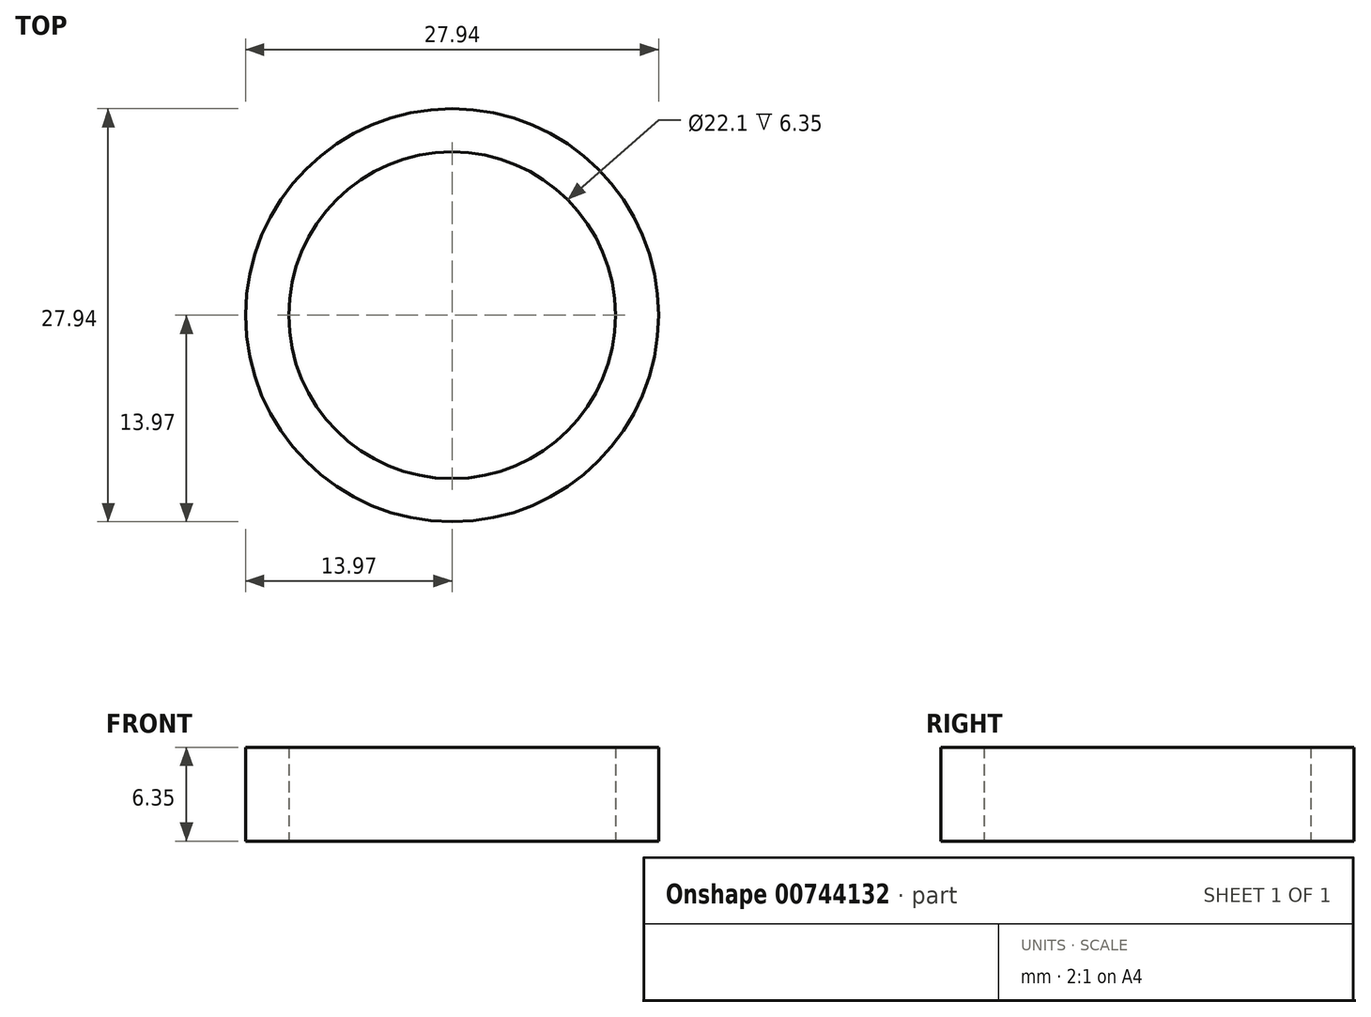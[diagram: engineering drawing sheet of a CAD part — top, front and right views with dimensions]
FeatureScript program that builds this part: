
annotation { "Feature Type Name" : "Feature", "Feature Type Description" : "" }
export const myFeature = defineFeature(function(context is Context, id is Id, definition is map)
    precondition{}
    {
        {
            var Q0;
            Q0=qCreatedBy(makeId("Top.planeOp"),FACE);
            var sketch = newSketch(context, id + "F0", { "sketchPlane" : qUnion([Q0])});
            skCircle(sketch, "E0", {"center": v(0, 0) * mm, "radius": 11.05 * mm});
            skCircle(sketch, "E1", {"center": v(0, 0) * mm, "radius": 13.97 * mm});
            skSolve(sketch);
        }
        {
            var Q0;
            Q0 = qSketchRegion(id + "F0", true);
            extrude(context, id + "F1", {"entities" : qUnion([Q0]), "depth" : 6.35 * mm, "offsetDistance" : 25.4 * mm});
        }
    });
